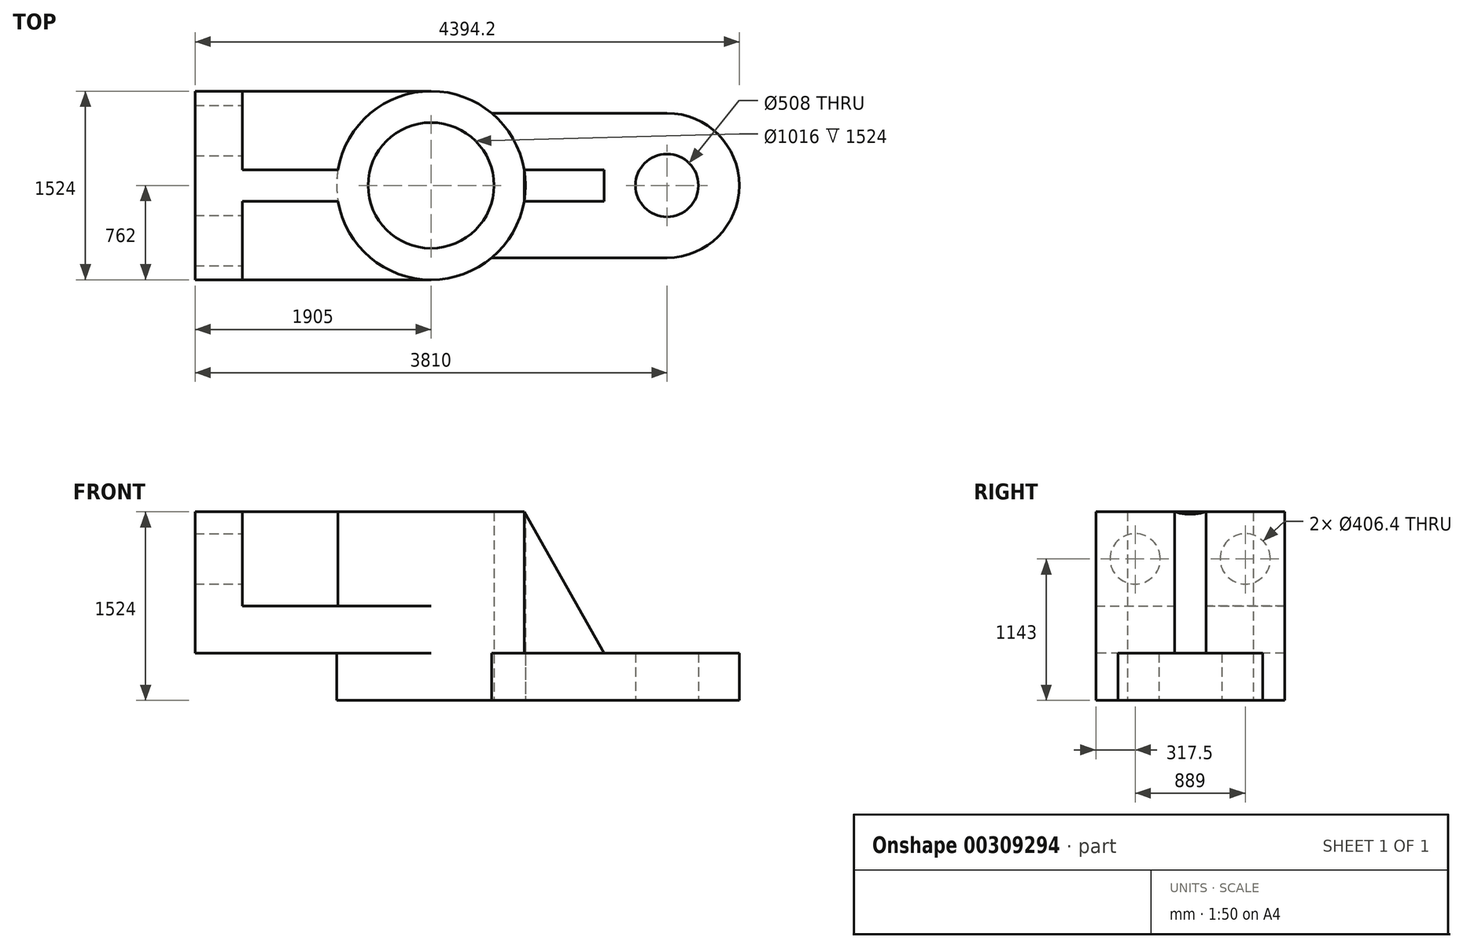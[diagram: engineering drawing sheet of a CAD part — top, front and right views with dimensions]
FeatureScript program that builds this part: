
annotation { "Feature Type Name" : "Feature", "Feature Type Description" : "" }
export const myFeature = defineFeature(function(context is Context, id is Id, definition is map)
    precondition{}
    {
        {
            var Q0;
            Q0=qCreatedBy(makeId("Top.planeOp"),FACE);
            var sketch = newSketch(context, id + "F0", { "sketchPlane" : qUnion([Q0])});
            skCircle(sketch, "E0", {"center": v(0, 0) * mm, "radius": 762 * mm});
            skCircle(sketch, "E1", {"center": v(0, 0) * mm, "radius": 508 * mm});
            skSolve(sketch);
        }
        {
            var Q0;
            Q0 = qSketchRegion(id + "F0", true);
            extrude(context, id + "F1", {"entities" : qUnion([Q0]), "depth" : 1524 * mm});
        }
        {
            var Q0;
            Q0=makeQuery(id+"F1.opExtrude","CAP_FACE",FACE,{"disambiguationData":[OSD([sQuery(id+"F0.wireOp",EDGE,"E0"),sQuery(id+"F0.wireOp",EDGE,"E1")])],"isStart":true});
            var sketch = newSketch(context, id + "F2", { "sketchPlane" : qUnion([Q0])});
            skCircle(sketch, "E2", {"center": v(1905, 0) * mm, "radius": 254 * mm});
            skCircle(sketch, "E3", {"center": v(1905, 0) * mm, "radius": 584.2 * mm});
            skLineSegment(sketch, "E4", {"start": v(1905, -584.2) * mm, "end": v(489.24, -584.2) * mm});
            skLineSegment(sketch, "E5", {"start": v(1905, 584.2) * mm, "end": v(489.24, 584.2) * mm});
            skSolve(sketch);
        }
        {
            var Q0;
            Q0 = qSketchRegion(id + "F2", true);
            var Q1;
            {var subQ0=sQuery(id+"F2.wireOp",EDGE,"E4");Q1=makeQuery(id+"F2.imprint","IMPRINT",FACE,{"disambiguationData":[TD([[makeQuery(id+"F2.imprint","IMPRINT",EDGE,{"derivedFrom":subQ0}),-1.0]])]});}
            extrude(context, id + "F3", {"entities" : qUnion([Q0, Q1]), "oppositeDirection" : true, "depth" : 381 * mm});
        }
        {
            var Q0;
            Q0=makeQuery(id+"F3.opExtrude","CAP_FACE",FACE,{"disambiguationData":[OSD([sQuery(id+"F0.wireOp",EDGE,"E0"),sQuery(id+"F2.wireOp",EDGE,"E2"),sQuery(id+"F2.wireOp",EDGE,"E3"),sQuery(id+"F2.wireOp",EDGE,"E4"),sQuery(id+"F2.wireOp",EDGE,"E5")])],"isStart":false});
            var sketch = newSketch(context, id + "F4", { "sketchPlane" : qUnion([Q0])});
            skLineSegment(sketch, "E6", {"start": v(762, 0) * mm, "end": v(1397, 0) * mm});
            skLineSegment(sketch, "E7", {"start": v(1397, 0) * mm, "end": v(1397, -127) * mm});
            skLineSegment(sketch, "E8", {"start": v(1397, -127) * mm, "end": v(1397, 127) * mm});
            skLineSegment(sketch, "E9", {"start": v(1397, 127) * mm, "end": v(751.34, 127) * mm});
            skLineSegment(sketch, "E10", {"start": v(1397, -127) * mm, "end": v(751.34, -127) * mm});
            skSolve(sketch);
        }
        {
            var Q0;
            {var subQ0=sQuery(id+"F4.wireOp",EDGE,"E6");Q0=makeQuery(id+"F4.imprint","IMPRINT",FACE,{"disambiguationData":[TD([[makeQuery(id+"F4.imprint","IMPRINT",EDGE,{"derivedFrom":subQ0}),-1.0]])]});}
            var Q1;
            {var subQ0=sQuery(id+"F4.wireOp",EDGE,"E6");Q1=makeQuery(id+"F4.imprint","IMPRINT",FACE,{"disambiguationData":[TD([[makeQuery(id+"F4.imprint","IMPRINT",EDGE,{"derivedFrom":subQ0}),1.0]])]});}
            extrude(context, id + "F5", {"entities" : qUnion([Q0, Q1]), "depth" : 1143 * mm});
        }
        {
            var Q0;
            Q0=makeQuery(id+"F5.opExtrude","SWEPT_FACE",FACE,{"disambiguationData":[OSD([sQuery(id+"F4.wireOp",EDGE,"E10")])]});
            var sketch = newSketch(context, id + "F6", { "sketchPlane" : qUnion([Q0])});
            skLineSegment(sketch, "E11", {"start": v(751.34, 1524) * mm, "end": v(1397, 381) * mm});
            skLineSegment(sketch, "E12", {"start": v(1397, 381) * mm, "end": v(1397, 1524) * mm});
            skLineSegment(sketch, "E13", {"start": v(1397, 1524) * mm, "end": v(751.34, 1524) * mm});
            skSolve(sketch);
        }
        {
            var Q0;
            Q0=makeQuery(id+"F6.imprint","IMPRINT",FACE,{"disambiguationData":[TD([[makeQuery(id+"F6.imprint","IMPRINT",EDGE,{"derivedFrom":sQuery(id+"F6.wireOp",EDGE,"E11")}),1.0]])]});
            extrude(context, id + "F7", {"entities" : qUnion([Q0]), "operationType" : NewBodyOperationType.REMOVE, "endBound" : BoundingType.THROUGH_ALL, "oppositeDirection" : true, "depth" : 25.4 * mm});
        }
        {
            var Q0;
            Q0=makeQuery(id+"F1.opExtrude","CAP_FACE",FACE,{"disambiguationData":[OSD([sQuery(id+"F0.wireOp",EDGE,"E0"),sQuery(id+"F0.wireOp",EDGE,"E1")])],"isStart":false});
            var sketch = newSketch(context, id + "F8", { "sketchPlane" : qUnion([Q0])});
            skLineSegment(sketch, "E14", {"start": v(-1905, 0) * mm, "end": v(-1905, 762) * mm});
            skLineSegment(sketch, "E15", {"start": v(-1905, 0) * mm, "end": v(-1905, -762) * mm});
            skLineSegment(sketch, "E16", {"start": v(-1905, -762) * mm, "end": v(-1524, -762) * mm});
            skLineSegment(sketch, "E17", {"start": v(-1524, -762) * mm, "end": v(-1524, -127) * mm});
            skLineSegment(sketch, "E18", {"start": v(-1524, -127) * mm, "end": v(-751.34, -127) * mm});
            skLineSegment(sketch, "E19", {"start": v(-1905, 762) * mm, "end": v(-1524, 762) * mm});
            skLineSegment(sketch, "E20", {"start": v(-1524, 762) * mm, "end": v(-1524, 127) * mm});
            skLineSegment(sketch, "E21", {"start": v(-1524, 127) * mm, "end": v(-751.34, 127) * mm});
            skSolve(sketch);
        }
        {
            var Q0;
            Q0=makeQuery(id+"F8.imprint","IMPRINT",FACE,{"disambiguationData":[TD([[makeQuery(id+"F8.imprint","IMPRINT",EDGE,{"derivedFrom":sQuery(id+"F8.wireOp",EDGE,"E14")}),-1.0]])]});
            extrude(context, id + "F9", {"entities" : qUnion([Q0]), "operationType" : NewBodyOperationType.ADD, "oppositeDirection" : true, "depth" : 1143 * mm});
        }
        {
            var Q0;
            Q0=makeQuery(id+"F9.opExtrude","CAP_FACE",FACE,{"disambiguationData":[OSD([sQuery(id+"F0.wireOp",EDGE,"E0"),sQuery(id+"F8.wireOp",EDGE,"E14"),sQuery(id+"F8.wireOp",EDGE,"E15"),sQuery(id+"F8.wireOp",EDGE,"E16"),sQuery(id+"F8.wireOp",EDGE,"E17"),sQuery(id+"F8.wireOp",EDGE,"E18"),sQuery(id+"F8.wireOp",EDGE,"E19"),sQuery(id+"F8.wireOp",EDGE,"E20"),sQuery(id+"F8.wireOp",EDGE,"E21")])],"isStart":false});
            var sketch = newSketch(context, id + "F10", { "sketchPlane" : qUnion([Q0])});
            skCircle(sketch, "E22.0.0", {"center": v(0, 0) * mm, "radius": 762 * mm});
            skLineSegment(sketch, "E23", {"start": v(-1524, 762) * mm, "end": v(0, 762) * mm});
            skLineSegment(sketch, "E24", {"start": v(-1524, -762) * mm, "end": v(0, -762) * mm});
            skSolve(sketch);
        }
        {
            var Q0;
            {var subQ2=sQuery(id+"F10.wireOp",EDGE,"E23");Q0=makeQuery(id+"F10.imprint","IMPRINT",FACE,{"disambiguationData":[TD([[makeQuery(id+"F10.imprint","IMPRINT",EDGE,{"derivedFrom":subQ2}),-1.0]])]});}
            var Q1;
            {var subQ2=sQuery(id+"F10.wireOp",EDGE,"E24");Q1=makeQuery(id+"F10.imprint","IMPRINT",FACE,{"disambiguationData":[TD([[makeQuery(id+"F10.imprint","IMPRINT",EDGE,{"derivedFrom":subQ2}),1.0]])]});}
            extrude(context, id + "F11", {"entities" : qUnion([Q0, Q1]), "operationType" : NewBodyOperationType.ADD, "oppositeDirection" : true, "depth" : 381 * mm});
        }
        {
            var Q0;
            Q0=makeQuery(id+"F9.opExtrude","SWEPT_FACE",FACE,{"disambiguationData":[OSD([sQuery(id+"F8.wireOp",EDGE,"E17")])]});
            var sketch = newSketch(context, id + "F12", { "sketchPlane" : qUnion([Q0])});
            skCircle(sketch, "E25", {"center": v(-444.5, 1143) * mm, "radius": 203.2 * mm});
            skPoint(sketch, "E25.centerSnap0", {"position": v(-762, 1143) * mm});
            skPoint(sketch, "E25.centerSnap1", {"position": v(-444.5, 1524) * mm});
            skSolve(sketch);
        }
        {
            var Q0;
            Q0=makeQuery(id+"F12.imprint","IMPRINT",FACE,{"disambiguationData":[TD([[makeQuery(id+"F12.imprint","IMPRINT",EDGE,{"derivedFrom":sQuery(id+"F12.wireOp",EDGE,"E25")}),1.0]])]});
            extrude(context, id + "F13", {"entities" : qUnion([Q0]), "operationType" : NewBodyOperationType.REMOVE, "endBound" : BoundingType.THROUGH_ALL, "oppositeDirection" : true, "depth" : 25.4 * mm});
        }
        {
            var Q0;
            Q0=makeQuery(id+"F9.opExtrude","SWEPT_FACE",FACE,{"disambiguationData":[OSD([sQuery(id+"F8.wireOp",EDGE,"E20")])]});
            var sketch = newSketch(context, id + "F14", { "sketchPlane" : qUnion([Q0])});
            skCircle(sketch, "E26", {"center": v(444.5, 1143) * mm, "radius": 203.2 * mm});
            skPoint(sketch, "E26.centerSnap0", {"position": v(444.5, 1524) * mm});
            skPoint(sketch, "E26.centerSnap1", {"position": v(762, 1143) * mm});
            skSolve(sketch);
        }
        {
            var Q0;
            Q0 = qSketchRegion(id + "F14", true);
            extrude(context, id + "F15", {"entities" : qUnion([Q0]), "operationType" : NewBodyOperationType.REMOVE, "endBound" : BoundingType.THROUGH_ALL, "oppositeDirection" : true, "depth" : 25.4 * mm});
        }
    });
